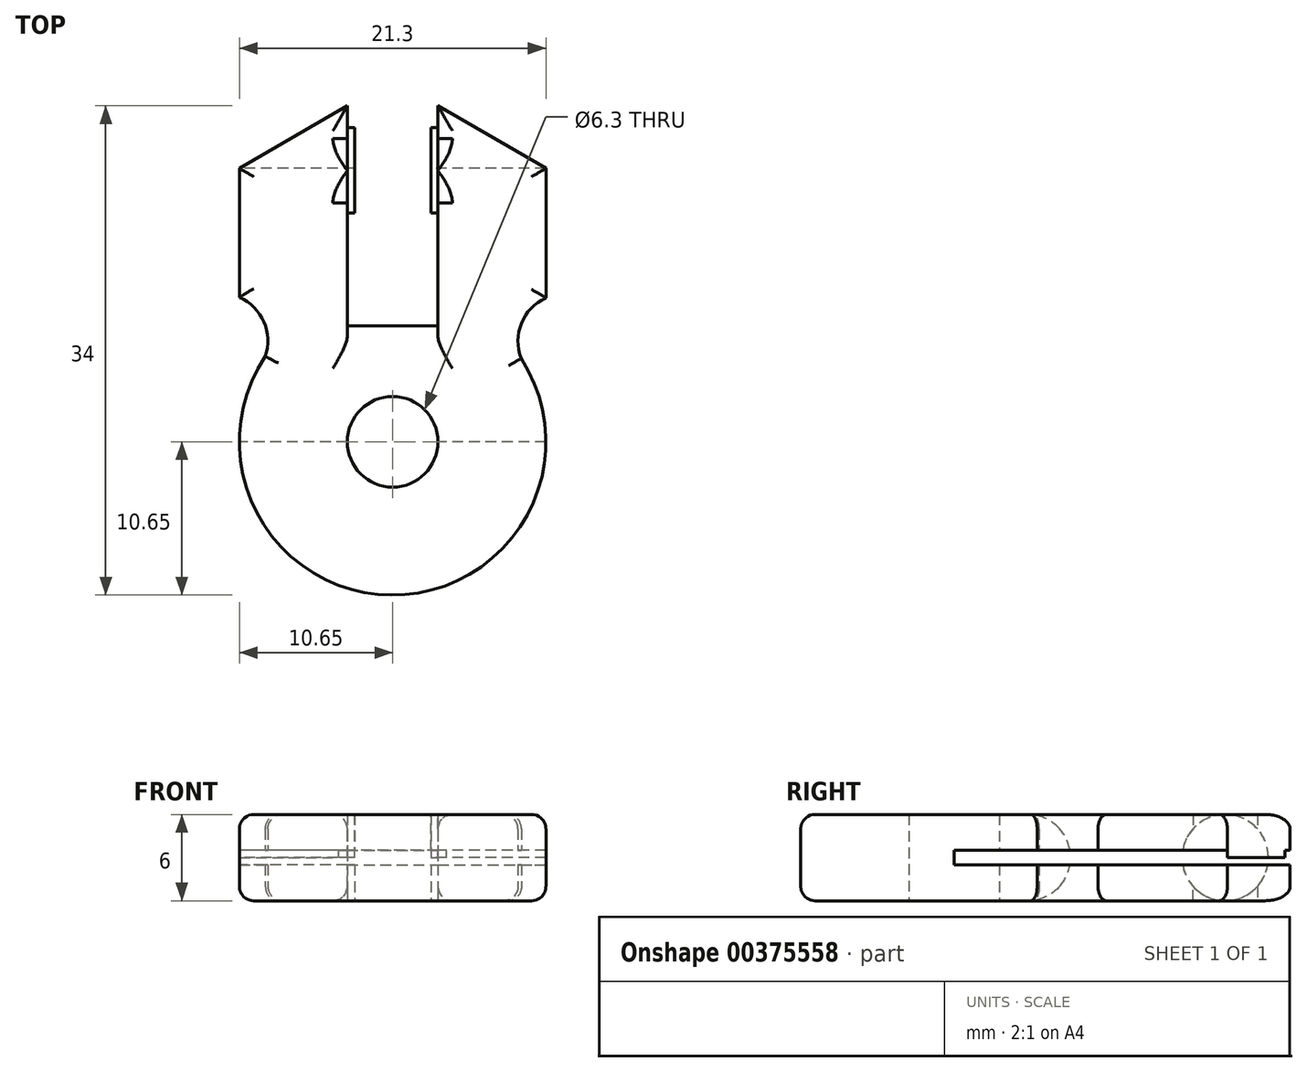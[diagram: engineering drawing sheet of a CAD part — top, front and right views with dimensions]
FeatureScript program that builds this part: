
annotation { "Feature Type Name" : "Feature", "Feature Type Description" : "" }
export const myFeature = defineFeature(function(context is Context, id is Id, definition is map)
    precondition{}
    {
        {
            var Q0;
            Q0=qCreatedBy(makeId("Top.planeOp"),FACE);
            var sketch = newSketch(context, id + "F0", { "sketchPlane" : qUnion([Q0])});
            skCircle(sketch, "E0", {"center": v(0, 0) * mm, "radius": 10.65 * mm});
            skCircle(sketch, "E1", {"center": v(0, 0) * mm, "radius": 3.15 * mm});
            skLineSegment(sketch, "E2", {"start": v(0, 0) * mm, "end": v(0, 8.1) * mm});
            skLineSegment(sketch, "E3", {"start": v(0, 8.1) * mm, "end": v(3.15, 8.1) * mm});
            skLineSegment(sketch, "E4", {"start": v(0, 8.1) * mm, "end": v(-3.15, 8.1) * mm});
            skLineSegment(sketch, "E5", {"start": v(-3.15, 8.1) * mm, "end": v(-3.15, 23.35) * mm});
            skLineSegment(sketch, "E6", {"start": v(3.15, 8.1) * mm, "end": v(3.15, 23.35) * mm});
            skLineSegment(sketch, "E7", {"start": v(10.65, 19) * mm, "end": v(3.15, 23.35) * mm});
            skLineSegment(sketch, "E8", {"start": v(10.65, 19) * mm, "end": v(10.65, 10) * mm});
            skLineSegment(sketch, "E9", {"start": v(-10.65, 19) * mm, "end": v(-3.15, 23.35) * mm});
            skLineSegment(sketch, "E10", {"start": v(-10.65, 19) * mm, "end": v(-10.65, 10) * mm});
            skLineSegment(sketch, "E11", {"start": v(0, 0) * mm, "end": v(-10.65, 0) * mm});
            skArc(sketch, "E12", {"start": v(-8.85, 5.93) * mm, "mid": v(-8.95, 8.34) * mm, "end": v(-10.65, 10.04) * mm});
            skLineSegment(sketch, "E13", {"start": v(0, 0) * mm, "end": v(10.65, 0) * mm});
            skArc(sketch, "E14", {"start": v(10.65, 10) * mm, "mid": v(8.95, 8.23) * mm, "end": v(8.94, 5.78) * mm});
            skSolve(sketch);
        }
        {
            var Q0;
            {var subQ0=sQuery(id+"F0.wireOp",EDGE,"E7");Q0=makeQuery(id+"F0.imprint","IMPRINT",FACE,{"disambiguationData":[TD([[makeQuery(id+"F0.imprint","IMPRINT",EDGE,{"derivedFrom":subQ0}),1.0]])]});}
            var Q1;
            {var subQ9=sQuery(id+"F0.wireOp",EDGE,"E3");Q1=makeQuery(id+"F0.imprint","IMPRINT",FACE,{"disambiguationData":[TD([[makeQuery(id+"F0.imprint","IMPRINT",EDGE,{"derivedFrom":subQ9}),-1.0]])]});}
            var Q2;
            {var subQ0=sQuery(id+"F0.wireOp",EDGE,"E4");Q2=makeQuery(id+"F0.imprint","IMPRINT",FACE,{"disambiguationData":[TD([[makeQuery(id+"F0.imprint","IMPRINT",EDGE,{"derivedFrom":subQ0}),1.0]])]});}
            var Q3;
            {var subQ0=sQuery(id+"F0.wireOp",EDGE,"E11");var subQ1=sQuery(id+"F0.wireOp",EDGE,"E0");var subQ2=makeQuery(id+"F0.imprint","INTERSECT",VERTEX,{"derivedFrom":[subQ1,subQ0]});Q3=makeQuery(id+"F0.imprint","IMPRINT",FACE,{"disambiguationData":[TD([[makeQuery(id+"F0.imprint","IMPRINT",EDGE,{"disambiguationData":[TD([[subQ2,-1.0]])],"derivedFrom":subQ1}),1.0]])]});}
            var Q4;
            {var subQ1=sQuery(id+"F0.wireOp",EDGE,"E9");Q4=makeQuery(id+"F0.imprint","IMPRINT",FACE,{"disambiguationData":[TD([[makeQuery(id+"F0.imprint","IMPRINT",EDGE,{"derivedFrom":subQ1}),-1.0]])]});}
            extrude(context, id + "F1", {"entities" : qUnion([Q0, Q1, Q2, Q3, Q4]), "depth" : 6 * mm});
        }
        {
            var Q0;
            Q0=makeQuery(id+"F1.opExtrude","SWEPT_FACE",FACE,{"disambiguationData":[OSD([sQuery(id+"F0.wireOp",EDGE,"E5")])]});
            var sketch = newSketch(context, id + "F2", { "sketchPlane" : qUnion([Q0])});
            skLineSegment(sketch, "E15", {"start": v(23.35, 0) * mm, "end": v(21.85, 0) * mm});
            skLineSegment(sketch, "E16", {"start": v(21.85, 0) * mm, "end": v(18.85, 0) * mm});
            skLineSegment(sketch, "E17", {"start": v(18.85, 0) * mm, "end": v(18.85, 3) * mm});
            skCircle(sketch, "E18", {"center": v(18.85, 3) * mm, "radius": 3 * mm});
            skSolve(sketch);
        }
        {
            var Q0;
            Q0 = qSketchRegion(id + "F2", true);
            extrude(context, id + "F3", {"entities" : qUnion([Q0]), "operationType" : NewBodyOperationType.ADD, "depth" : .5 * mm});
        }
        {
            var Q0;
            Q0=makeQuery(id+"F1.opExtrude","SWEPT_FACE",FACE,{"disambiguationData":[OSD([sQuery(id+"F0.wireOp",EDGE,"E6")])]});
            var sketch = newSketch(context, id + "F4", { "sketchPlane" : qUnion([Q0])});
            skLineSegment(sketch, "E19", {"start": v(-23.35, 0) * mm, "end": v(-18.85, 0) * mm});
            skLineSegment(sketch, "E20", {"start": v(-18.85, 0) * mm, "end": v(-18.85, 3) * mm});
            skCircle(sketch, "E21", {"center": v(-18.85, 3) * mm, "radius": 3 * mm});
            skSolve(sketch);
        }
        {
            var Q0;
            {var subQ0=sQuery(id+"F4.wireOp",EDGE,"E21");var subQ1=sQuery(id+"F0.wireOp",EDGE,"E6");var subQ3=makeQuery(id+"F4.imprint","INTERSECT",VERTEX,{"derivedFrom":[makeQuery(id+"F1.opExtrude","CAP_EDGE",EDGE,{"disambiguationData":[OSD([subQ1])],"isStart":false}),subQ0]});Q0=makeQuery(id+"F4.imprint","IMPRINT",FACE,{"disambiguationData":[TD([[makeQuery(id+"F4.imprint","IMPRINT",EDGE,{"disambiguationData":[TD([[subQ3,-1.0]])],"derivedFrom":subQ0}),1.0]])]});}
            extrude(context, id + "F5", {"entities" : qUnion([Q0]), "operationType" : NewBodyOperationType.ADD, "depth" : .5 * mm});
        }
        {
            var Q0;
            Q0=makeQuery(id+"F1.opExtrude","CAP_EDGE",EDGE,{"disambiguationData":[OSD([sQuery(id+"F0.wireOp",EDGE,"E3"),sQuery(id+"F0.wireOp",EDGE,"E4")])],"isStart":false});
            fillet(context, id + "F6", {"entities" : qUnion([Q0]), "radius" : 3 * mm, "tangentPropagation" : true, "allowEdgeOverflow" : false});
        }
        {
            var Q0;
            Q0=makeQuery(id+"F1.opExtrude","CAP_EDGE",EDGE,{"disambiguationData":[OSD([sQuery(id+"F0.wireOp",EDGE,"E3"),sQuery(id+"F0.wireOp",EDGE,"E4")])],"isStart":true});
            fillet(context, id + "F7", {"entities" : qUnion([Q0]), "radius" : 3 * mm, "tangentPropagation" : true, "allowEdgeOverflow" : false});
        }
        {
            var Q0;
            Q0=makeQuery(id+"F1.opExtrude","SWEPT_FACE",FACE,{"disambiguationData":[OSD([sQuery(id+"F0.wireOp",EDGE,"E10")])]});
            var sketch = newSketch(context, id + "F8", { "sketchPlane" : qUnion([Q0])});
            skLineSegment(sketch, "E22", {"start": v(-19, 0) * mm, "end": v(-19, 3) * mm});
            skLineSegment(sketch, "E23", {"start": v(-19, 3) * mm, "end": v(-23, 3) * mm});
            skLineSegment(sketch, "E24.bottom", {"start": v(-23, 3) * mm, "end": v(-10.04, 3) * mm});
            skLineSegment(sketch, "E24.left", {"start": v(-23, 3) * mm, "end": v(-23, 2.5) * mm});
            skLineSegment(sketch, "E25.left", {"start": v(-23, 3) * mm, "end": v(-23, 3.5) * mm});
            skLineSegment(sketch, "E26", {"start": v(-10.04, 3) * mm, "end": v(0, 3) * mm});
            skLineSegment(sketch, "E27.bottom", {"start": v(-23, 2.5) * mm, "end": v(0, 2.5) * mm});
            skLineSegment(sketch, "E27.top", {"start": v(-23, 3) * mm, "end": v(0, 3) * mm});
            skLineSegment(sketch, "E27.left", {"start": v(-23, 2.5) * mm, "end": v(-23, 3) * mm});
            skLineSegment(sketch, "E27.right", {"start": v(0, 2.5) * mm, "end": v(0, 3) * mm});
            skLineSegment(sketch, "E28.bottom", {"start": v(0, 3) * mm, "end": v(-23, 3) * mm});
            skLineSegment(sketch, "E28.top", {"start": v(0, 3.5) * mm, "end": v(-23, 3.5) * mm});
            skLineSegment(sketch, "E28.left", {"start": v(0, 3) * mm, "end": v(0, 3.5) * mm});
            skLineSegment(sketch, "E29.bottom", {"start": v(-23, 2.5) * mm, "end": v(-24.27, 2.5) * mm});
            skLineSegment(sketch, "E29.top", {"start": v(-23, 3.5) * mm, "end": v(-24.27, 3.5) * mm});
            skLineSegment(sketch, "E29.left", {"start": v(-23, 2.5) * mm, "end": v(-23, 3.5) * mm});
            skLineSegment(sketch, "E29.right", {"start": v(-24.27, 2.5) * mm, "end": v(-24.27, 3.5) * mm});
            skSolve(sketch);
        }
        {
            var Q0;
            {var subQ0=sQuery(id+"F8.wireOp",EDGE,"E27.right");Q0=makeQuery(id+"F8.imprint","IMPRINT",FACE,{"disambiguationData":[TD([[makeQuery(id+"F8.imprint","IMPRINT",EDGE,{"derivedFrom":subQ0}),1.0]])]});}
            var Q1;
            {var subQ0=sQuery(id+"F8.wireOp",EDGE,"E28.left");Q1=makeQuery(id+"F8.imprint","IMPRINT",FACE,{"disambiguationData":[TD([[makeQuery(id+"F8.imprint","IMPRINT",EDGE,{"derivedFrom":subQ0}),1.0]])]});}
            var Q2;
            {var subQ1=sQuery(id+"F0.wireOp",EDGE,"E10");var subQ4=makeQuery(id+"F1.opExtrude","SWEPT_EDGE",EDGE,{"disambiguationData":[OSD([subQ1,sQuery(id+"F0.wireOp",EDGE,"E12")])]});var subQ6=sQuery(id+"F8.wireOp",EDGE,"E28.top");var subQ7=makeQuery(id+"F8.imprint","INTERSECT",VERTEX,{"derivedFrom":[subQ4,subQ6]});Q2=makeQuery(id+"F8.imprint","IMPRINT",FACE,{"disambiguationData":[TD([[makeQuery(id+"F8.imprint","IMPRINT",EDGE,{"disambiguationData":[TD([[subQ7,-1.0]])],"derivedFrom":subQ6}),1.0]])]});}
            var Q3;
            {var subQ1=sQuery(id+"F8.wireOp",EDGE,"E22");var subQ4=sQuery(id+"F8.wireOp",EDGE,"E27.bottom");var subQ5=makeQuery(id+"F8.imprint","INTERSECT",VERTEX,{"derivedFrom":[subQ1,subQ4]});Q3=makeQuery(id+"F8.imprint","IMPRINT",FACE,{"disambiguationData":[TD([[makeQuery(id+"F8.imprint","IMPRINT",EDGE,{"disambiguationData":[TD([[subQ5,-1.0]])],"derivedFrom":subQ4}),1.0]])]});}
            var Q4;
            {var subQ0=sQuery(id+"F8.wireOp",EDGE,"E28.bottom");var subQ3=sQuery(id+"F8.wireOp",EDGE,"E29.left");var subQ4=makeQuery(id+"F8.imprint","INTERSECT",VERTEX,{"derivedFrom":[subQ0,subQ3]});Q4=makeQuery(id+"F8.imprint","IMPRINT",FACE,{"disambiguationData":[TD([[makeQuery(id+"F8.imprint","IMPRINT",EDGE,{"disambiguationData":[TD([[subQ4,-1.0]])],"derivedFrom":subQ3}),-1.0]])]});}
            var Q5;
            {var subQ1=sQuery(id+"F8.wireOp",EDGE,"E22");var subQ3=sQuery(id+"F8.wireOp",EDGE,"E27.bottom");var subQ4=makeQuery(id+"F8.imprint","INTERSECT",VERTEX,{"derivedFrom":[subQ1,subQ3]});Q5=makeQuery(id+"F8.imprint","IMPRINT",FACE,{"disambiguationData":[TD([[makeQuery(id+"F8.imprint","IMPRINT",EDGE,{"disambiguationData":[TD([[subQ4,1.0]])],"derivedFrom":subQ3}),1.0]])]});}
            var Q6;
            {var subQ3=sQuery(id+"F8.wireOp",EDGE,"E29.bottom");Q6=makeQuery(id+"F8.imprint","IMPRINT",FACE,{"disambiguationData":[TD([[makeQuery(id+"F8.imprint","IMPRINT",EDGE,{"derivedFrom":subQ3}),-1.0]])]});}
            extrude(context, id + "F9", {"entities" : qUnion([Q0, Q1, Q2, Q3, Q4, Q5, Q6]), "operationType" : NewBodyOperationType.REMOVE, "oppositeDirection" : true, "depth" : 25 * mm});
        }
        {
            var Q0;
            Q0=makeQuery(id+"F1.opExtrude","CAP_EDGE",EDGE,{"disambiguationData":[OSD([sQuery(id+"F0.wireOp",EDGE,"E0")])],"isStart":false});
            var Q1;
            Q1=makeQuery(id+"F1.opExtrude","CAP_EDGE",EDGE,{"disambiguationData":[OSD([sQuery(id+"F0.wireOp",EDGE,"E12")])],"isStart":false});
            var Q2;
            Q2=makeQuery(id+"F1.opExtrude","CAP_EDGE",EDGE,{"disambiguationData":[OSD([sQuery(id+"F0.wireOp",EDGE,"E10")])],"isStart":false});
            var Q3;
            Q3=makeQuery(id+"F1.opExtrude","CAP_EDGE",EDGE,{"disambiguationData":[OSD([sQuery(id+"F0.wireOp",EDGE,"E9")])],"isStart":false});
            var Q4;
            {var subQ0=sQuery(id+"F0.wireOp",EDGE,"E5");var subQ1=sQuery(id+"F0.wireOp",EDGE,"E4");var subQ2=sQuery(id+"F0.wireOp",EDGE,"E3");Q4=makeQuery(id+"F3.boolean.opBoolean","SPLIT",EDGE,{"disambiguationData":[TD([makeQuery(id+"F1.opExtrude","SWEPT_FACE",FACE,{"disambiguationData":[OSD([subQ2,subQ1])]})])],"derivedFrom":makeQuery(id+"F1.opExtrude","CAP_EDGE",EDGE,{"disambiguationData":[OSD([subQ0])],"isStart":false})});}
            var Q5;
            {var subQ0=sQuery(id+"F0.wireOp",EDGE,"E9");var subQ1=sQuery(id+"F0.wireOp",EDGE,"E5");Q5=makeQuery(id+"F3.boolean.opBoolean","SPLIT",EDGE,{"disambiguationData":[TD([makeQuery(id+"F1.opExtrude","SWEPT_FACE",FACE,{"disambiguationData":[OSD([subQ0])]})])],"derivedFrom":makeQuery(id+"F1.opExtrude","CAP_EDGE",EDGE,{"disambiguationData":[OSD([subQ1])],"isStart":false})});}
            var Q6;
            {var subQ0=sQuery(id+"F0.wireOp",EDGE,"E6");var subQ1=sQuery(id+"F0.wireOp",EDGE,"E4");var subQ2=sQuery(id+"F0.wireOp",EDGE,"E3");Q6=makeQuery(id+"F5.boolean.opBoolean","SPLIT",EDGE,{"disambiguationData":[TD([makeQuery(id+"F1.opExtrude","SWEPT_FACE",FACE,{"disambiguationData":[OSD([subQ2,subQ1])]})])],"derivedFrom":makeQuery(id+"F1.opExtrude","CAP_EDGE",EDGE,{"disambiguationData":[OSD([subQ0])],"isStart":false})});}
            var Q7;
            {var subQ0=sQuery(id+"F0.wireOp",EDGE,"E7");var subQ1=sQuery(id+"F0.wireOp",EDGE,"E6");Q7=makeQuery(id+"F5.boolean.opBoolean","SPLIT",EDGE,{"disambiguationData":[TD([makeQuery(id+"F1.opExtrude","SWEPT_FACE",FACE,{"disambiguationData":[OSD([subQ0])]})])],"derivedFrom":makeQuery(id+"F1.opExtrude","CAP_EDGE",EDGE,{"disambiguationData":[OSD([subQ1])],"isStart":false})});}
            var Q8;
            Q8=makeQuery(id+"F1.opExtrude","CAP_EDGE",EDGE,{"disambiguationData":[OSD([sQuery(id+"F0.wireOp",EDGE,"E7")])],"isStart":false});
            var Q9;
            Q9=makeQuery(id+"F1.opExtrude","CAP_EDGE",EDGE,{"disambiguationData":[OSD([sQuery(id+"F0.wireOp",EDGE,"E8")])],"isStart":false});
            var Q10;
            Q10=makeQuery(id+"F1.opExtrude","CAP_EDGE",EDGE,{"disambiguationData":[OSD([sQuery(id+"F0.wireOp",EDGE,"E14")])],"isStart":false});
            var Q11;
            Q11=makeQuery(id+"F1.opExtrude","CAP_EDGE",EDGE,{"disambiguationData":[OSD([sQuery(id+"F0.wireOp",EDGE,"E0")])],"isStart":true});
            var Q12;
            Q12=makeQuery(id+"F1.opExtrude","CAP_EDGE",EDGE,{"disambiguationData":[OSD([sQuery(id+"F0.wireOp",EDGE,"E10")])],"isStart":true});
            var Q13;
            Q13=makeQuery(id+"F1.opExtrude","CAP_EDGE",EDGE,{"disambiguationData":[OSD([sQuery(id+"F0.wireOp",EDGE,"E12")])],"isStart":true});
            var Q14;
            Q14=makeQuery(id+"F1.opExtrude","CAP_EDGE",EDGE,{"disambiguationData":[OSD([sQuery(id+"F0.wireOp",EDGE,"E9")])],"isStart":true});
            var Q15;
            {var subQ0=sQuery(id+"F0.wireOp",EDGE,"E6");var subQ1=sQuery(id+"F0.wireOp",EDGE,"E4");var subQ2=sQuery(id+"F0.wireOp",EDGE,"E3");Q15=makeQuery(id+"F5.boolean.opBoolean","SPLIT",EDGE,{"disambiguationData":[TD([makeQuery(id+"F1.opExtrude","SWEPT_FACE",FACE,{"disambiguationData":[OSD([subQ2,subQ1])]})])],"derivedFrom":makeQuery(id+"F1.opExtrude","CAP_EDGE",EDGE,{"disambiguationData":[OSD([subQ0])],"isStart":true})});}
            var Q16;
            {var subQ0=sQuery(id+"F0.wireOp",EDGE,"E5");var subQ1=sQuery(id+"F0.wireOp",EDGE,"E4");var subQ2=sQuery(id+"F0.wireOp",EDGE,"E3");Q16=makeQuery(id+"F3.boolean.opBoolean","SPLIT",EDGE,{"disambiguationData":[TD([makeQuery(id+"F1.opExtrude","SWEPT_FACE",FACE,{"disambiguationData":[OSD([subQ2,subQ1])]})])],"derivedFrom":makeQuery(id+"F1.opExtrude","CAP_EDGE",EDGE,{"disambiguationData":[OSD([subQ0])],"isStart":true})});}
            var Q17;
            {var subQ0=sQuery(id+"F0.wireOp",EDGE,"E9");var subQ1=sQuery(id+"F0.wireOp",EDGE,"E5");Q17=makeQuery(id+"F3.boolean.opBoolean","SPLIT",EDGE,{"disambiguationData":[TD([makeQuery(id+"F1.opExtrude","SWEPT_FACE",FACE,{"disambiguationData":[OSD([subQ0])]})])],"derivedFrom":makeQuery(id+"F1.opExtrude","CAP_EDGE",EDGE,{"disambiguationData":[OSD([subQ1])],"isStart":true})});}
            var Q18;
            Q18=makeQuery(id+"F1.opExtrude","CAP_EDGE",EDGE,{"disambiguationData":[OSD([sQuery(id+"F0.wireOp",EDGE,"E7")])],"isStart":true});
            var Q19;
            Q19=makeQuery(id+"F1.opExtrude","CAP_EDGE",EDGE,{"disambiguationData":[OSD([sQuery(id+"F0.wireOp",EDGE,"E8")])],"isStart":true});
            var Q20;
            Q20=makeQuery(id+"F1.opExtrude","CAP_EDGE",EDGE,{"disambiguationData":[OSD([sQuery(id+"F0.wireOp",EDGE,"E14")])],"isStart":true});
            var Q21;
            {var subQ0=sQuery(id+"F0.wireOp",EDGE,"E7");var subQ1=sQuery(id+"F0.wireOp",EDGE,"E6");Q21=makeQuery(id+"F5.boolean.opBoolean","SPLIT",EDGE,{"disambiguationData":[TD([makeQuery(id+"F1.opExtrude","SWEPT_FACE",FACE,{"disambiguationData":[OSD([subQ0])]})])],"derivedFrom":makeQuery(id+"F1.opExtrude","CAP_EDGE",EDGE,{"disambiguationData":[OSD([subQ1])],"isStart":true})});}
            fillet(context, id + "F10", {"entities" : qUnion([Q0, Q1, Q2, Q3, Q4, Q5, Q6, Q7, Q8, Q9, Q10, Q11, Q12, Q13, Q14, Q15, Q16, Q17, Q18, Q19, Q20, Q21]), "radius" : 1 * mm, "tangentPropagation" : true, "allowEdgeOverflow" : false});
        }
    });
